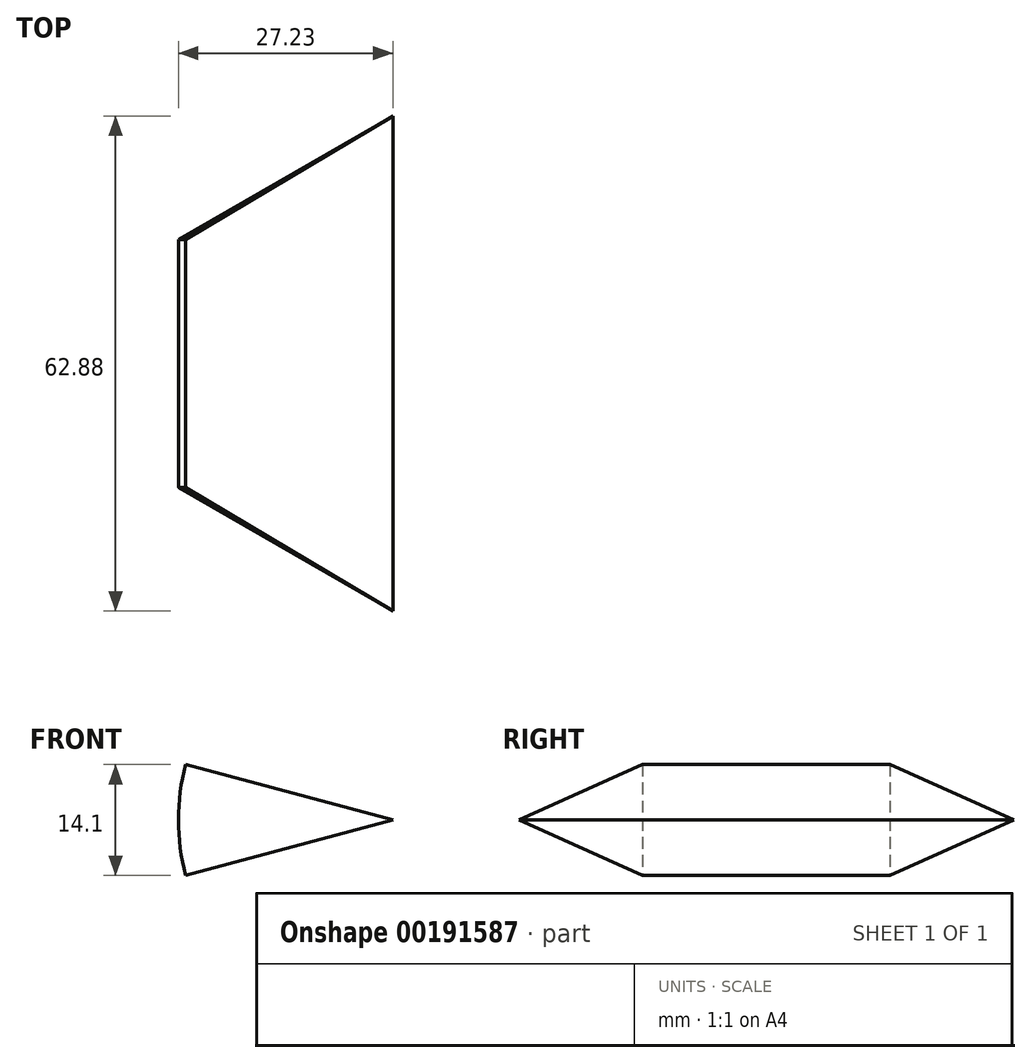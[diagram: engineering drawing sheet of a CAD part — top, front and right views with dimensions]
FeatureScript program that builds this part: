
annotation { "Feature Type Name" : "Feature", "Feature Type Description" : "" }
export const myFeature = defineFeature(function(context is Context, id is Id, definition is map)
    precondition{}
    {
        {
            var Q0;
            Q0=qCreatedBy(makeId("Top.planeOp"),FACE);
            var sketch = newSketch(context, id + "F0", { "sketchPlane" : qUnion([Q0])});
            skLineSegment(sketch, "E0", {"start": v(0, -75.72) * mm, "end": v(0, 74.93) * mm});
            skArc(sketch, "E1.cCircle", {"start": v(0, 27.23) * mm, "mid": v(-27.23, 0) * mm, "end": v(0, -27.23) * mm, "construction": true});
            skLineSegment(sketch, "E1.2", {"start": v(0, -31.44) * mm, "end": v(-27.23, -15.72) * mm});
            skLineSegment(sketch, "E1.3", {"start": v(-27.23, -15.72) * mm, "end": v(-27.23, 15.72) * mm});
            skLineSegment(sketch, "E1.4", {"start": v(-27.23, 15.72) * mm, "end": v(0, 31.44) * mm});
            skPoint(sketch, "E1.0.midPoint", {"position": v(27.23, 0) * mm});
            skPoint(sketch, "E2.orphan", {"position": v(27.23, 15.72) * mm});
            skPoint(sketch, "E1.1.start.orphan", {"position": v(27.23, -15.72) * mm});
            skSolve(sketch);
        }
        {
            var Q0;
            {var subQ0=sQuery(id+"F0.wireOp",EDGE,"E1.2");Q0=makeQuery(id+"F0.imprint","IMPRINT",FACE,{"disambiguationData":[TD([[makeQuery(id+"F0.imprint","IMPRINT",EDGE,{"derivedFrom":subQ0}),-1.0]])]});}
            var Q1;
            Q1=sQuery(id+"F0.wireOp",EDGE,"E0");
            revolve(context, id + "F1", {"entities" : qUnion([Q0]), "axis" : qUnion([Q1]), "revolveType" : RevolveType.SYMMETRIC, "angle" : 30 * degree});
        }
    });
